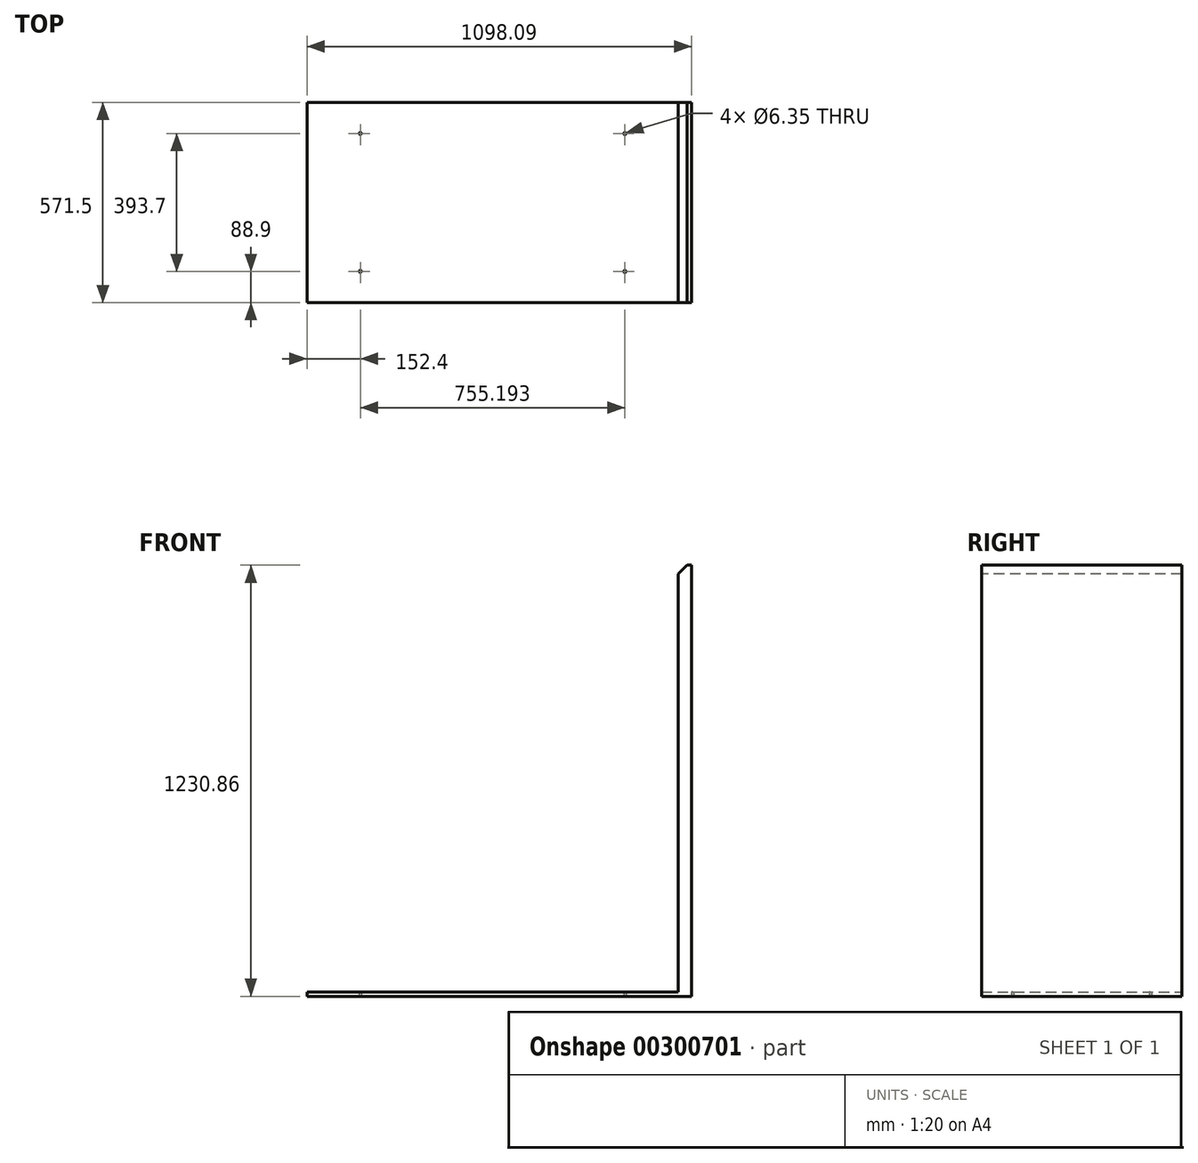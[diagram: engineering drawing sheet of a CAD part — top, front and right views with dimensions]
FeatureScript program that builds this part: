
annotation { "Feature Type Name" : "Feature", "Feature Type Description" : "" }
export const myFeature = defineFeature(function(context is Context, id is Id, definition is map)
    precondition{}
    {
        {
            var Q0;
            Q0=qCreatedBy(makeId("Top.planeOp"),FACE);
            var sketch = newSketch(context, id + "F0", { "sketchPlane" : qUnion([Q0])});
            skLineSegment(sketch, "E0", {"start": v(0, 0) * mm, "end": v(1098.1, 0) * mm});
            skLineSegment(sketch, "E1", {"start": v(1098.1, 0) * mm, "end": v(1098.1, 571.5) * mm});
            skLineSegment(sketch, "E2", {"start": v(1098.1, 571.5) * mm, "end": v(0, 571.5) * mm});
            skLineSegment(sketch, "E3", {"start": v(0, 571.5) * mm, "end": v(0, 0) * mm});
            skPoint(sketch, "E4", {"position": v(152.4, 482.6) * mm});
            skPoint(sketch, "E5", {"position": v(907.6, 482.6) * mm});
            skPoint(sketch, "E6", {"position": v(152.4, 88.9) * mm});
            skPoint(sketch, "E7", {"position": v(907.6, 88.9) * mm});
            skSolve(sketch);
        }
        {
            var Q0;
            Q0 = qSketchRegion(id + "F0", true);
            extrude(context, id + "F1", {"entities" : qUnion([Q0]), "depth" : 12.65 * mm});
        }
        {
            var Q0;
            Q0=makeQuery(id+"F1.opExtrude","CAP_FACE",FACE,{"disambiguationData":[OSD([sQuery(id+"F0.wireOp",EDGE,"E0"),sQuery(id+"F0.wireOp",EDGE,"E1"),sQuery(id+"F0.wireOp",EDGE,"E2"),sQuery(id+"F0.wireOp",EDGE,"E3")])],"isStart":false});
            var sketch = newSketch(context, id + "F2", { "sketchPlane" : qUnion([Q0])});
            skLineSegment(sketch, "E8", {"start": v(1098.1, 571.5) * mm, "end": v(1098.1, 0) * mm});
            skLineSegment(sketch, "E9", {"start": v(1098.1, 0) * mm, "end": v(1060, 0) * mm});
            skLineSegment(sketch, "E10", {"start": v(1060, 0) * mm, "end": v(1060, 571.5) * mm});
            skLineSegment(sketch, "E11", {"start": v(1060, 571.5) * mm, "end": v(1098.1, 571.5) * mm});
            skSolve(sketch);
        }
        {
            var Q0;
            Q0 = qSketchRegion(id + "F2", true);
            extrude(context, id + "F3", {"entities" : qUnion([Q0]), "operationType" : NewBodyOperationType.ADD, "depth" : 1218.2 * mm});
        }
        {
            var Q0;
            Q0=makeQuery(id+"F3.boolean.opBoolean","MERGE",FACE,{"derivedFrom":[makeQuery(id+"F1.opExtrude","SWEPT_FACE",FACE,{"disambiguationData":[OSD([sQuery(id+"F0.wireOp",EDGE,"E0")])]}),makeQuery(id+"F3.opExtrude","SWEPT_FACE",FACE,{"disambiguationData":[OSD([sQuery(id+"F2.wireOp",EDGE,"E9")])]})]});
            var sketch = newSketch(context, id + "F4", { "sketchPlane" : qUnion([Q0])});
            skLineSegment(sketch, "E12", {"start": v(1085.4, 1230.86) * mm, "end": v(1060, 1205.46) * mm});
            skSolve(sketch);
        }
        {
            var Q0;
            Q0 = qSketchRegion(id + "F4", true);
            var Q1;
            {var subQ0=sQuery(id+"F4.wireOp",EDGE,"E12");Q1=makeQuery(id+"F4.imprint","IMPRINT",FACE,{"disambiguationData":[TD([[makeQuery(id+"F4.imprint","IMPRINT",EDGE,{"derivedFrom":subQ0}),-1.0]])]});}
            extrude(context, id + "F5", {"entities" : qUnion([Q0, Q1]), "operationType" : NewBodyOperationType.REMOVE, "oppositeDirection" : true, "depth" : 1270 * mm});
        }
        {
            var Q0;
            Q0=sQuery(id+"F0.wireOp",VERTEX,"E4");
            var Q1;
            Q1=sQuery(id+"F0.wireOp",VERTEX,"E5");
            var Q2;
            Q2=sQuery(id+"F0.wireOp",VERTEX,"E7");
            var Q3;
            Q3=sQuery(id+"F0.wireOp",VERTEX,"E6");
            var Q4;
            Q4=makeQuery(id+"F1.opExtrude","SWEPT_BODY",BODY,{"disambiguationData":[OSD([sQuery(id+"F0.wireOp",EDGE,"E0"),sQuery(id+"F0.wireOp",EDGE,"E1"),sQuery(id+"F0.wireOp",EDGE,"E2"),sQuery(id+"F0.wireOp",EDGE,"E3")])]});
            hole(context, id + "F6", {"style" : HoleStyle.SIMPLE, "endStyle" : HoleEndStyle.BLIND, "oppositeDirection" : true, "holeDiameter" : 6.35 * mm, "holeDepth" : 25.4 * mm, "tappedDepth" : 12.7 * mm, "tapClearance" : 3, "locations" : qUnion([Q0, Q1, Q2, Q3]), "scope" : qUnion([Q4])});
        }
    });
